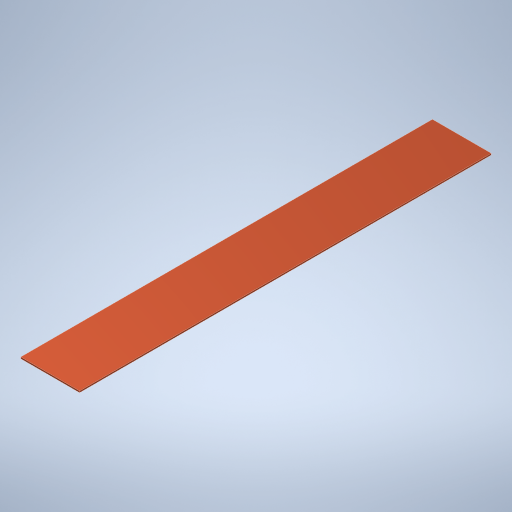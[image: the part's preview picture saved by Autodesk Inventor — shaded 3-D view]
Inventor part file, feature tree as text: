
AUTODESK INVENTOR PART (.ipt)
format: ipt  version: 2023 (Build 270158000, 158)  size: 228,864 bytes
history: native  units: in
note: dims shown in document units (in); Inventor stores cm internally (conversion verified against a paired STEP export)
features: extrude x1, sketch x1
ambient origin geometry x8: Origin, YZ Plane, XZ Plane, XY Plane, X Axis, Y Axis, Z Axis, Center Point
bodies: Solid1 (feature_tree)
feature tree (2):
  extrude  "Extrusion1"  Depth=0.3937in
  sketch  "Sketch1"  dims[d0=2.7559in d1=0.3937in d2=0.01in d3=0.0in]
